# Revit family: Mounted_Storage_&_Accessories-Teknion-PAX_Personal_Organizers-R2019
name_source: partatom
category: Furniture
units: mm (PartAtom-declared; Revit-internal decimal feet)

## family parameters
Always vertical = Yes
Cut with Voids When Loaded = No
OmniClass Number = 23.40.20.00
OmniClass Title = General Furniture and Specialties
Room Calculation Point = No
Shared = Yes
Work Plane-Based = Yes

## types (11) — shared parameters
Assembly Code = E2020200
Default Elevation = 48 "
Manufacturer = Teknion
Manufacturer Fax = 416.661.4586
Part Number = PAX
Product Documentation Link = https://www.teknion.com
Product Line = Expansion Desking
Product Page URL = https://www.teknion.com
Series = Expansion Desking
Sustainability Data = https://www.teknion.com
URL = www.teknion.com
Unit Weight URL = http://www.teknion.com
Warranty = http://www.teknion.com

## per-type parameters (varying)
| type | Depth | Description | Height | Model | Width |
| Divisional Sorter, Legal | 3.401 " | Personal Organizers, Divisional Sorter, Legal | 5.57 " | PAX91 | 12.548 " |
| Divisional Sorter, Letter/A4 | 3.401 " | Personal Organizers, Divisional Sorter, Letter/A4 | 5.57 " | PAX90 | 9.548 " |
| Tray, Letter/A4 | 10.785 " | Personal Organizers, Tray, Letter/A4 | 0 " | PAX92 | 8.673 " |
| Tray, Legal | 13.785 " | Personal Organizers, Tray, Legal | 0 " | PAX93 | 8.673 " |
| Pencil Tray | 10.605 " | Personal Organizers, Pencil Tray | 0 " | PAX94 | 3 " |
| Binder Bin | 4 " | Personal Organizers, Binder Bin | 0 " | PAX95 | 8.598 " |
| Media Organizer | 4 " | Personal Organizers, Media Organizer | 0 " | PAX96 | 5.048 " |
| Telephone Shelf, Small | 9 " | Personal Organizers, Telephone Shelf, Small | 0 " | PAX97 | 9.895 " |
| Telephone Shelf, Large | 13 " | Personal Organizers, Telephone Shelf, Large | 0 " | PAX98 | 9.6 " |
| Vertical Organizer, Letter/A4 | 12.5 " | Personal Organizers, Vertical Organizer, Letter/A4 | 0 " | PAX99 | 1 " |
| Vertical Organizer, Legal | 15 " | Personal Organizers, Vertical Organizer, Legal | 0 " | PAX100 | 1 " |

type visibility flags: 11 boolean params named "<type name>" — each type sets only its own to Yes (folded from table)

## geometry (parser evidence)
native form markers: Sweep x28
no freeform markers — native parametric forms only
